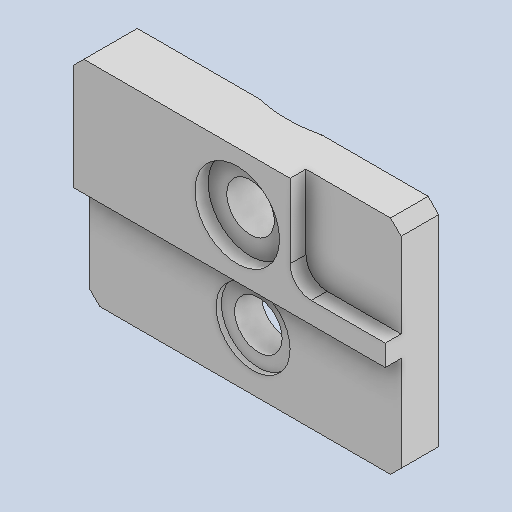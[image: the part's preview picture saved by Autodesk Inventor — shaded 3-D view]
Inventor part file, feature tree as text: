
AUTODESK INVENTOR PART (.ipt)
format: ipt  version: 2024.2 (Build 282272000, 272)  size: 264,704 bytes
history: native  units: in
note: dims shown in document units (in); Inventor stores cm internally (conversion verified against a paired STEP export)
features: extrude x7, hole x3, chamfer x1
ambient origin geometry x8: Origin, YZ Plane, XZ Plane, XY Plane, X Axis, Y Axis, Z Axis, Center Point
bodies: Solid1 (feature_tree)
feature tree (11):
  extrude  "Extrusion1"  Depth=1.1614in
  extrude  "Extrusion2"  Depth=0.8268in
  hole  "Hole1"  [1 undecoded]
  hole  "Hole2"  [1 undecoded]
  hole  "Hole3"  [1 undecoded]
  extrude  "Extrusion3"  Depth=1.1614in
  extrude  "Extrusion4"  TaperAngle=0.0deg  [1 undecoded]
  chamfer  "Chamfer3"  Distance=0.0591in
  extrude  "Extrusion5"  TaperAngle=0.0deg  [1 undecoded]
  extrude  "Extrusion6"  Depth=0.1772in
  extrude  "Extrusion7"  TaperAngle=0.0deg  [1 undecoded]
note: 6 required parameter values undecoded (feature->parameter linkage not recoverable at this tier; creation-order binding heuristic only, values carry confidence <= 0.55)
